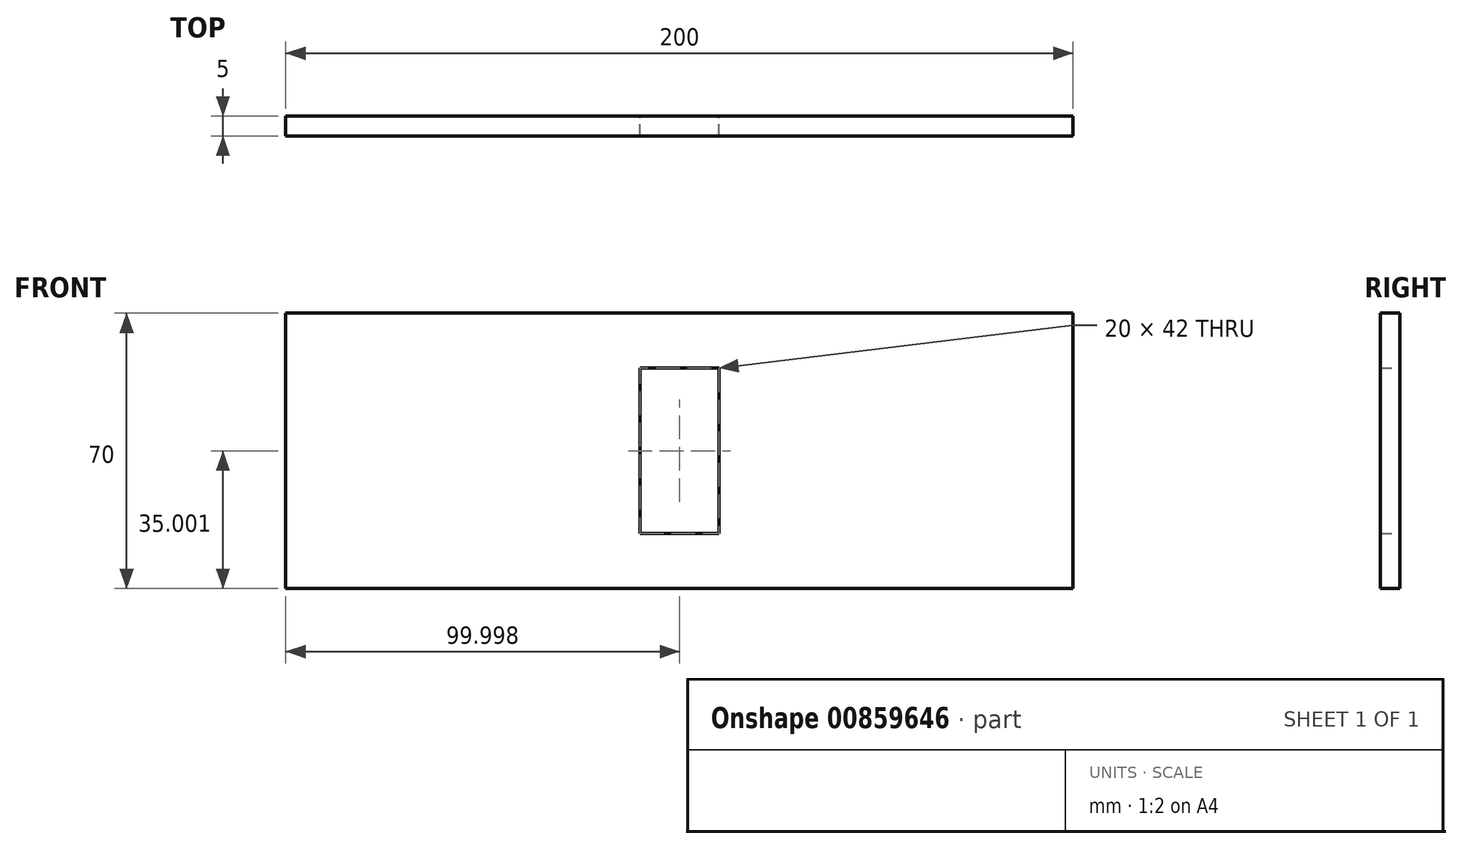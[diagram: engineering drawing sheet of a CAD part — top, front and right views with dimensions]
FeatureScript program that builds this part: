
annotation { "Feature Type Name" : "Feature", "Feature Type Description" : "" }
export const myFeature = defineFeature(function(context is Context, id is Id, definition is map)
    precondition{}
    {
        {
            var Q0;
            Q0=qCreatedBy(makeId("Front.planeOp"),FACE);
            var sketch = newSketch(context, id + "F0", { "sketchPlane" : qUnion([Q0])});
            skLineSegment(sketch, "E0.bottom", {"start": v(123.19, -13.22) * mm, "end": v(-76.81, -13.22) * mm});
            skLineSegment(sketch, "E0.top", {"start": v(123.19, -83.22) * mm, "end": v(-76.81, -83.22) * mm});
            skLineSegment(sketch, "E0.left", {"start": v(123.19, -13.22) * mm, "end": v(123.19, -83.22) * mm});
            skLineSegment(sketch, "E0.right", {"start": v(-76.81, -13.22) * mm, "end": v(-76.81, -83.22) * mm});
            skLineSegment(sketch, "E1.bottom", {"start": v(33.19, -69.22) * mm, "end": v(13.19, -69.22) * mm});
            skLineSegment(sketch, "E1.top", {"start": v(33.19, -27.22) * mm, "end": v(13.19, -27.22) * mm});
            skLineSegment(sketch, "E1.left", {"start": v(33.19, -69.22) * mm, "end": v(33.19, -27.22) * mm});
            skLineSegment(sketch, "E1.right", {"start": v(13.19, -69.22) * mm, "end": v(13.19, -27.22) * mm});
            skPoint(sketch, "E1.middle", {"position": v(23.19, -48.22) * mm});
            skSolve(sketch);
        }
        {
            var Q0;
            Q0=makeQuery(id+"F0.imprint","IMPRINT",FACE,{"disambiguationData":[TD([[makeQuery(id+"F0.imprint","IMPRINT",EDGE,{"derivedFrom":sQuery(id+"F0.wireOp",EDGE,"E0.bottom")}),1.0]])]});
            extrude(context, id + "F1", {"entities" : qUnion([Q0]), "depth" : 5 * mm, "offsetDistance" : 25 * mm});
        }
    });
